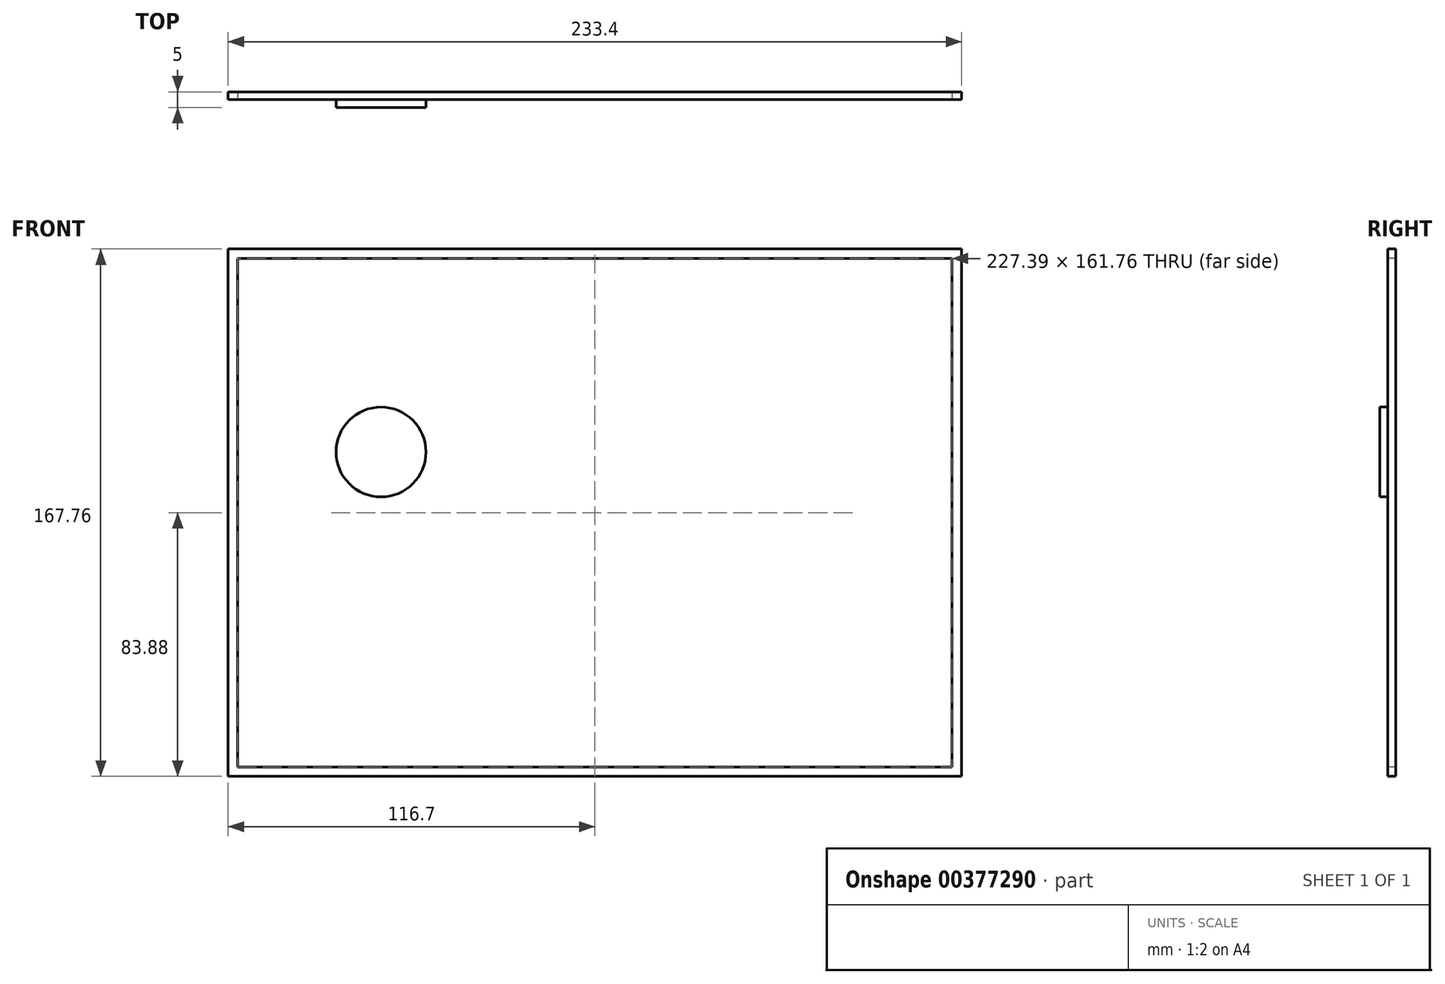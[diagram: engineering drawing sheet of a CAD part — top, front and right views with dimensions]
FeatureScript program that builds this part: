
annotation { "Feature Type Name" : "Feature", "Feature Type Description" : "" }
export const myFeature = defineFeature(function(context is Context, id is Id, definition is map)
    precondition{}
    {
        {
            var Q0;
            Q0=qCreatedBy(makeId("Front.planeOp"),FACE);
            var sketch = newSketch(context, id + "F0", { "sketchPlane" : qUnion([Q0])});
            skCircle(sketch, "E0", {"center": v(-68.03, 19.3) * mm, "radius": 14.29 * mm});
            skCircle(sketch, "E1", {"center": v(-17.6, 58.6) * mm, "radius": 12.7 * mm});
            skCircle(sketch, "E2", {"center": v(20.7, 58.6) * mm, "radius": 12.7 * mm});
            skCircle(sketch, "E3", {"center": v(2.6, 18.23) * mm, "radius": 14.29 * mm});
            skCircle(sketch, "E4", {"center": v(40.76, 18.23) * mm, "radius": 14.29 * mm});
            skCircle(sketch, "E5", {"center": v(78.92, 18.23) * mm, "radius": 14.29 * mm});
            skCircle(sketch, "E6", {"center": v(2.59, -16.86) * mm, "radius": 14.29 * mm});
            skCircle(sketch, "E7", {"center": v(40.76, -16.86) * mm, "radius": 14.29 * mm});
            skCircle(sketch, "E8", {"center": v(78.94, -16.82) * mm, "radius": 14.26 * mm});
            skCircle(sketch, "E9", {"center": v(-17.46, -51.96) * mm, "radius": 14.29 * mm});
            skCircle(sketch, "E10", {"center": v(20.7, -51.96) * mm, "radius": 14.29 * mm});
            skLineSegment(sketch, "E11", {"start": v(-116.7, 83.88) * mm, "end": v(116.7, 83.88) * mm});
            skLineSegment(sketch, "E12", {"start": v(116.7, 83.88) * mm, "end": v(116.7, -83.88) * mm});
            skLineSegment(sketch, "E13", {"start": v(116.7, -83.88) * mm, "end": v(-116.7, -83.88) * mm});
            skLineSegment(sketch, "E14", {"start": v(-116.7, -83.88) * mm, "end": v(-116.7, 83.88) * mm});
            skSolve(sketch);
        }
        {
            var Q0;
            Q0=makeQuery(id+"F0.imprint","IMPRINT",FACE,{"disambiguationData":[TD([[makeQuery(id+"F0.imprint","IMPRINT",EDGE,{"derivedFrom":sQuery(id+"F0.wireOp",EDGE,"E0")}),1.0]])]});
            extrude(context, id + "F1", {"entities" : qUnion([Q0]), "depth" : 2.5 * mm});
        }
        {
            var Q0;
            Q0=makeQuery(id+"F1.opExtrude","CAP_FACE",FACE,{"disambiguationData":[OSD([sQuery(id+"F0.wireOp",EDGE,"E0"),sQuery(id+"F0.wireOp",EDGE,"E1"),sQuery(id+"F0.wireOp",EDGE,"E2"),sQuery(id+"F0.wireOp",EDGE,"E3"),sQuery(id+"F0.wireOp",EDGE,"E4"),sQuery(id+"F0.wireOp",EDGE,"E5"),sQuery(id+"F0.wireOp",EDGE,"E6"),sQuery(id+"F0.wireOp",EDGE,"E7"),sQuery(id+"F0.wireOp",EDGE,"E8"),sQuery(id+"F0.wireOp",EDGE,"E9"),sQuery(id+"F0.wireOp",EDGE,"E10"),sQuery(id+"F0.wireOp",EDGE,"E11"),sQuery(id+"F0.wireOp",EDGE,"E12"),sQuery(id+"F0.wireOp",EDGE,"E13"),sQuery(id+"F0.wireOp",EDGE,"E14")])],"isStart":true});
            var sketch = newSketch(context, id + "F2", { "sketchPlane" : qUnion([Q0])});
            skLineSegment(sketch, "E15.bottom", {"start": v(-116.7, -83.88) * mm, "end": v(116.7, -83.88) * mm});
            skLineSegment(sketch, "E15.top", {"start": v(-116.7, -80.88) * mm, "end": v(116.7, -80.88) * mm});
            skLineSegment(sketch, "E15.left", {"start": v(-116.7, -83.88) * mm, "end": v(-116.7, -80.88) * mm});
            skLineSegment(sketch, "E15.right", {"start": v(116.7, -83.88) * mm, "end": v(116.7, -80.88) * mm});
            skLineSegment(sketch, "E16.bottom", {"start": v(-116.7, 83.88) * mm, "end": v(116.7, 83.88) * mm});
            skLineSegment(sketch, "E16.top", {"start": v(-116.7, 80.88) * mm, "end": v(116.7, 80.88) * mm});
            skLineSegment(sketch, "E16.left", {"start": v(-116.7, 83.88) * mm, "end": v(-116.7, 80.88) * mm});
            skLineSegment(sketch, "E16.right", {"start": v(116.7, 83.88) * mm, "end": v(116.7, 80.88) * mm});
            skLineSegment(sketch, "E17.bottom", {"start": v(116.7, -83.88) * mm, "end": v(113.7, -83.88) * mm});
            skLineSegment(sketch, "E17.top", {"start": v(116.7, 83.88) * mm, "end": v(113.7, 83.88) * mm});
            skLineSegment(sketch, "E17.left", {"start": v(116.7, -83.88) * mm, "end": v(116.7, 83.88) * mm});
            skLineSegment(sketch, "E17.right", {"start": v(113.7, -83.88) * mm, "end": v(113.7, 83.88) * mm});
            skLineSegment(sketch, "E18.bottom", {"start": v(-116.7, -83.88) * mm, "end": v(-113.7, -83.88) * mm});
            skLineSegment(sketch, "E18.top", {"start": v(-116.7, 83.88) * mm, "end": v(-113.7, 83.88) * mm});
            skLineSegment(sketch, "E18.left", {"start": v(-116.7, -83.88) * mm, "end": v(-116.7, 83.88) * mm});
            skLineSegment(sketch, "E18.right", {"start": v(-113.7, -83.88) * mm, "end": v(-113.7, 83.88) * mm});
            skSolve(sketch);
        }
        {
            var Q0;
            Q0 = qSketchRegion(id + "F2", true);
            extrude(context, id + "F3", {"entities" : qUnion([Q0]), "operationType" : NewBodyOperationType.ADD, "depth" : 2.5 * mm});
        }
    });
